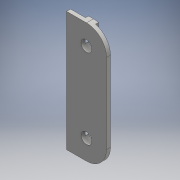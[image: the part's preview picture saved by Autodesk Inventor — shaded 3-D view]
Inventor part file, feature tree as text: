
AUTODESK INVENTOR PART (.ipt)
format: ipt  version: 2016 (Build 200138000, 138)  size: 119,808 bytes
history: native  units: mm
features: sketch x3, extrude x2, fillet x1, hole x1
ambient origin geometry x8: Origin, YZ Plane, XZ Plane, XY Plane, X Axis, Y Axis, Z Axis, Center Point
bodies: Solid1 (feature_tree)
feature tree (7):
  extrude  "Extrusion1"  Depth=60.0mm
  extrude  "Extrusion2"  Depth=5.0mm
  fillet  "Fillet1"  Radius=1.5mm
  hole  "Hole1"  [1 undecoded]
  sketch  "Sketch1"  dims[d0=20.0mm d1=60.0mm]
  sketch  "Sketch2"  dims[d2=2.0mm d3=0.0mm d4=5.0mm d5=1.5mm d6=0.0mm]
  sketch  "Sketch3"  dims[d7=10.0mm d8=5.5mm d9=6.0mm d10=4.0mm d11=2.0mm d12=90.0deg d13=8.0mm d14=20.594885mm]
note: 1 required parameter value undecoded (feature->parameter linkage not recoverable at this tier; creation-order binding heuristic only, values carry confidence <= 0.55)
